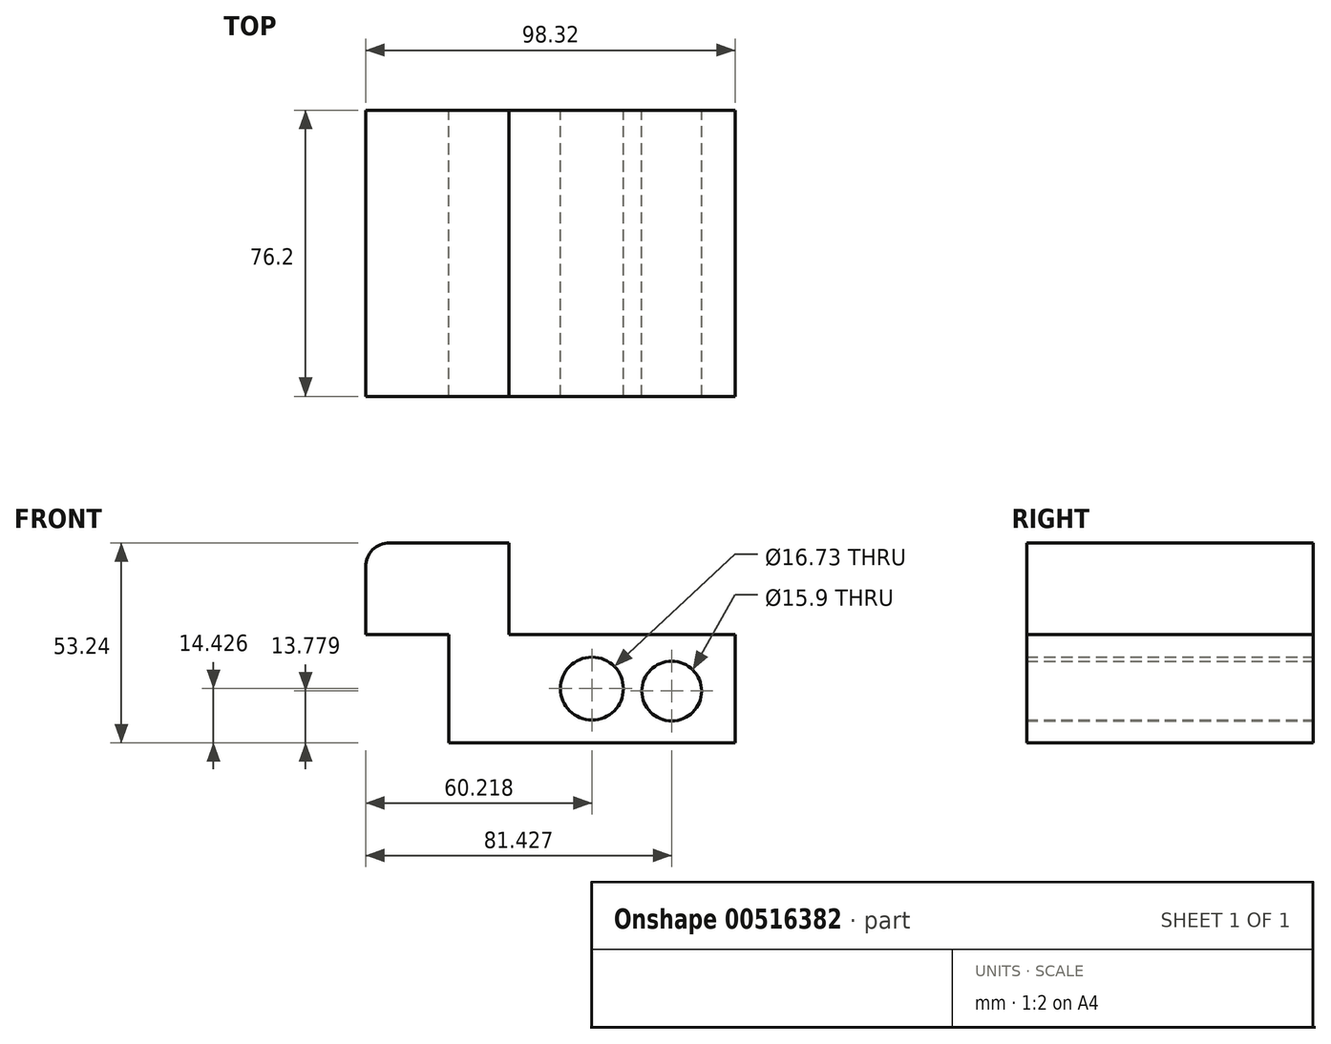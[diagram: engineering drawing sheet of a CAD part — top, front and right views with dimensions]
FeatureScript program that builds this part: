
annotation { "Feature Type Name" : "Feature", "Feature Type Description" : "" }
export const myFeature = defineFeature(function(context is Context, id is Id, definition is map)
    precondition{}
    {
        {
            var Q0;
            Q0=qCreatedBy(makeId("Front.planeOp"),FACE);
            var sketch = newSketch(context, id + "F0", { "sketchPlane" : qUnion([Q0])});
            skLineSegment(sketch, "E0.bottom", {"start": v(-4.22, 0) * mm, "end": v(71.98, 0) * mm});
            skLineSegment(sketch, "E0.top", {"start": v(-4.22, 28.85) * mm, "end": v(71.98, 28.85) * mm});
            skLineSegment(sketch, "E0.left", {"start": v(-4.22, 0) * mm, "end": v(-4.22, 28.85) * mm});
            skLineSegment(sketch, "E0.right", {"start": v(71.98, 0) * mm, "end": v(71.98, 28.85) * mm});
            skPoint(sketch, "E0.middle", {"position": v(33.88, 14.43) * mm});
            skLineSegment(sketch, "E1.bottom", {"start": v(-26.34, 28.85) * mm, "end": v(11.76, 28.85) * mm});
            skLineSegment(sketch, "E1.top", {"start": v(-20, 53.24) * mm, "end": v(11.76, 53.24) * mm});
            skLineSegment(sketch, "E1.left", {"start": v(-26.34, 28.85) * mm, "end": v(-26.34, 46.9) * mm});
            skLineSegment(sketch, "E1.right", {"start": v(11.76, 28.85) * mm, "end": v(11.76, 53.24) * mm});
            skPoint(sketch, "E1.middle", {"position": v(-7.3, 41.05) * mm});
            skPoint(sketch, "E2.visualSharp", {"position": v(-26.34, 53.24) * mm});
            skArc(sketch, "E2.filletArc", {"start": v(-20, 53.24) * mm, "mid": v(-24.48, 51.38) * mm, "end": v(-26.34, 46.9) * mm});
            skCircle(sketch, "E3", {"center": v(33.88, 14.43) * mm, "radius": 8.37 * mm});
            skPoint(sketch, "E4.middle", {"position": v(55.09, 13.78) * mm});
            skCircle(sketch, "E5", {"center": v(55.09, 13.78) * mm, "radius": 7.95 * mm});
            skSolve(sketch);
        }
        {
            var Q0;
            Q0=makeQuery(id+"F0.imprint","IMPRINT",FACE,{"disambiguationData":[TD([[makeQuery(id+"F0.imprint","IMPRINT",EDGE,{"derivedFrom":sQuery(id+"F0.wireOp",EDGE,"E0.bottom")}),1.0]])]});
            var Q1;
            Q1=makeQuery(id+"F0.imprint","IMPRINT",FACE,{"disambiguationData":[TD([[makeQuery(id+"F0.imprint","IMPRINT",EDGE,{"derivedFrom":sQuery(id+"F0.wireOp",EDGE,"E1.top")}),-1.0]])]});
            extrude(context, id + "F1", {"entities" : qUnion([Q0, Q1]), "depth" : 76.2 * mm, "offsetDistance" : 25.4 * mm});
        }
    });
